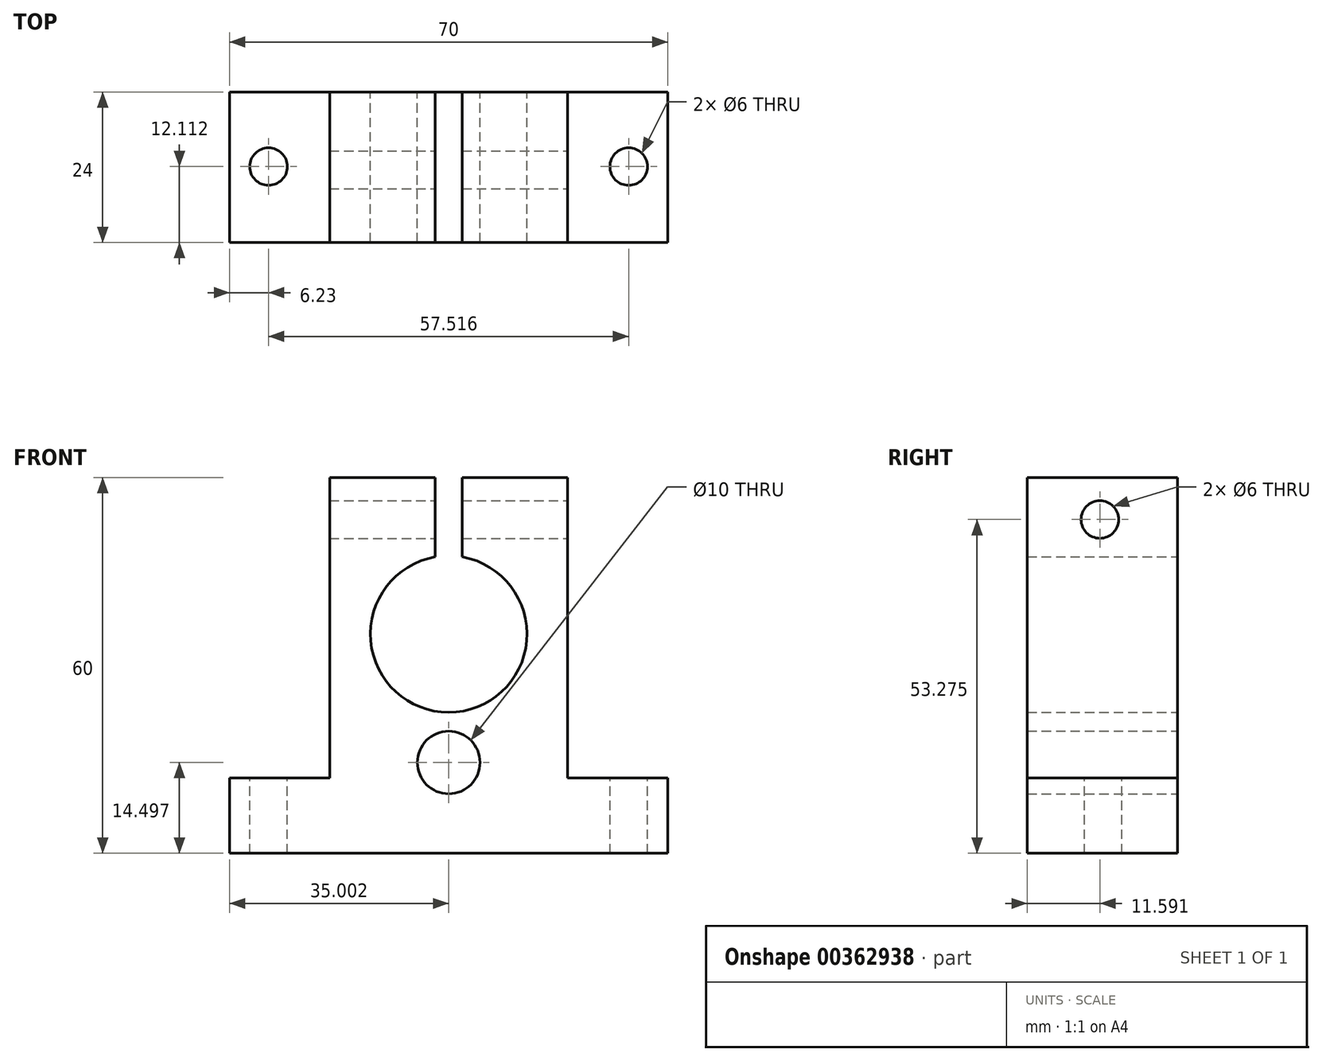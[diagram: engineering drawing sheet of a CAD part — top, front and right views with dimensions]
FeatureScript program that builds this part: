
annotation { "Feature Type Name" : "Feature", "Feature Type Description" : "" }
export const myFeature = defineFeature(function(context is Context, id is Id, definition is map)
    precondition{}
    {
        {
            var Q0;
            Q0=qCreatedBy(makeId("Front.planeOp"),FACE);
            var sketch = newSketch(context, id + "F0", { "sketchPlane" : qUnion([Q0])});
            skLineSegment(sketch, "E0.bottom", {"start": v(1.56, 38.65) * mm, "end": v(18.39, 38.65) * mm});
            skLineSegment(sketch, "E0.top", {"start": v(1.56, -21.35) * mm, "end": v(39.56, -21.35) * mm});
            skLineSegment(sketch, "E0.left", {"start": v(1.56, 38.65) * mm, "end": v(1.56, -9.35) * mm});
            skLineSegment(sketch, "E0.right", {"start": v(39.56, 38.65) * mm, "end": v(39.56, -9.35) * mm});
            skLineSegment(sketch, "E1", {"start": v(1.56, 13.65) * mm, "end": v(20.56, 13.65) * mm, "construction": true});
            skLineSegment(sketch, "E2", {"start": v(20.56, 13.65) * mm, "end": v(39.56, 13.65) * mm, "construction": true});
            skArc(sketch, "E3", {"start": v(18.39, 25.96) * mm, "mid": v(20.56, 1.15) * mm, "end": v(22.74, 25.96) * mm});
            skLineSegment(sketch, "E4", {"start": v(1.56, -21.35) * mm, "end": v(-14.44, -21.35) * mm});
            skLineSegment(sketch, "E5", {"start": v(39.56, -21.35) * mm, "end": v(55.56, -21.35) * mm});
            skLineSegment(sketch, "E6", {"start": v(-14.44, -21.35) * mm, "end": v(-14.44, -9.35) * mm});
            skLineSegment(sketch, "E7", {"start": v(-14.44, -9.35) * mm, "end": v(1.56, -9.35) * mm});
            skLineSegment(sketch, "E8.MirrorCS", {"start": v(55.56, -9.35) * mm, "end": v(39.56, -9.35) * mm});
            skLineSegment(sketch, "E9.MirrorCS", {"start": v(55.56, -21.35) * mm, "end": v(55.56, -9.35) * mm});
            skLineSegment(sketch, "E10", {"start": v(18.39, 38.65) * mm, "end": v(18.39, 25.96) * mm});
            skLineSegment(sketch, "E11.MirrorCS", {"start": v(22.74, 38.65) * mm, "end": v(22.74, 25.96) * mm});
            skLineSegment(sketch, "E12.trimOffspring", {"start": v(22.74, 38.65) * mm, "end": v(39.56, 38.65) * mm});
            skLineSegment(sketch, "E13", {"start": v(20.56, 13.65) * mm, "end": v(20.56, -39.3) * mm, "construction": true});
            skCircle(sketch, "E14", {"center": v(20.56, -6.85) * mm, "radius": 5 * mm});
            skSolve(sketch);
        }
        {
            var Q0;
            Q0=makeQuery(id+"F0.imprint","IMPRINT",FACE,{"disambiguationData":[TD([[makeQuery(id+"F0.imprint","IMPRINT",EDGE,{"derivedFrom":sQuery(id+"F0.wireOp",EDGE,"E0.bottom")}),-1.0]])]});
            extrude(context, id + "F1", {"entities" : qUnion([Q0]), "depth" : 24 * mm});
        }
        {
            var Q0;
            Q0=makeQuery(id+"F1.opExtrude","SWEPT_FACE",FACE,{"disambiguationData":[OSD([sQuery(id+"F0.wireOp",EDGE,"E0.right")])]});
            var sketch = newSketch(context, id + "F2", { "sketchPlane" : qUnion([Q0])});
            skCircle(sketch, "E15", {"center": v(-12.4, 31.93) * mm, "radius": 2.73 * mm});
            skSolve(sketch);
        }
        {
            var Q0;
            Q0=sQuery(id+"F2.wireOp",VERTEX,"E15.center");
            var Q1;
            Q1=makeQuery(id+"F1.opExtrude","SWEPT_BODY",BODY,{"disambiguationData":[OSD([sQuery(id+"F0.wireOp",EDGE,"E0.bottom"),sQuery(id+"F0.wireOp",EDGE,"E0.top"),sQuery(id+"F0.wireOp",EDGE,"E0.left"),sQuery(id+"F0.wireOp",EDGE,"E0.right"),sQuery(id+"F0.wireOp",EDGE,"E3"),sQuery(id+"F0.wireOp",EDGE,"E4"),sQuery(id+"F0.wireOp",EDGE,"E5"),sQuery(id+"F0.wireOp",EDGE,"E6"),sQuery(id+"F0.wireOp",EDGE,"E7"),sQuery(id+"F0.wireOp",EDGE,"E8.MirrorCS"),sQuery(id+"F0.wireOp",EDGE,"E9.MirrorCS"),sQuery(id+"F0.wireOp",EDGE,"E10"),sQuery(id+"F0.wireOp",EDGE,"E11.MirrorCS"),sQuery(id+"F0.wireOp",EDGE,"E12.trimOffspring")])]});
            hole(context, id + "F3", {"style" : HoleStyle.SIMPLE, "endStyle" : HoleEndStyle.THROUGH, "holeDiameter" : 6 * mm, "isTappedThrough" : true, "tappedDepth" : 12 * mm, "tapClearance" : 3, "locations" : qUnion([Q0]), "scope" : qUnion([Q1])});
        }
        {
            var Q0;
            Q0=makeQuery(id+"F1.opExtrude","SWEPT_FACE",FACE,{"disambiguationData":[OSD([sQuery(id+"F0.wireOp",EDGE,"E7")])]});
            var sketch = newSketch(context, id + "F4", { "sketchPlane" : qUnion([Q0])});
            skCircle(sketch, "E16", {"center": v(-8.2, -11.89) * mm, "radius": 3.02 * mm});
            skCircle(sketch, "E17.MirrorC", {"center": v(49.3, -11.89) * mm, "radius": 3.02 * mm});
            skSolve(sketch);
        }
        {
            var Q0;
            Q0=sQuery(id+"F4.wireOp",VERTEX,"E16.center");
            var Q1;
            Q1=sQuery(id+"F4.wireOp",VERTEX,"E17.MirrorC.center");
            var Q2;
            Q2=makeQuery(id+"F1.opExtrude","SWEPT_BODY",BODY,{"disambiguationData":[OSD([sQuery(id+"F0.wireOp",EDGE,"E0.bottom"),sQuery(id+"F0.wireOp",EDGE,"E0.top"),sQuery(id+"F0.wireOp",EDGE,"E0.left"),sQuery(id+"F0.wireOp",EDGE,"E0.right"),sQuery(id+"F0.wireOp",EDGE,"E3"),sQuery(id+"F0.wireOp",EDGE,"E4"),sQuery(id+"F0.wireOp",EDGE,"E5"),sQuery(id+"F0.wireOp",EDGE,"E6"),sQuery(id+"F0.wireOp",EDGE,"E7"),sQuery(id+"F0.wireOp",EDGE,"E8.MirrorCS"),sQuery(id+"F0.wireOp",EDGE,"E9.MirrorCS"),sQuery(id+"F0.wireOp",EDGE,"E10"),sQuery(id+"F0.wireOp",EDGE,"E11.MirrorCS"),sQuery(id+"F0.wireOp",EDGE,"E12.trimOffspring")])]});
            hole(context, id + "F5", {"style" : HoleStyle.SIMPLE, "endStyle" : HoleEndStyle.THROUGH, "holeDiameter" : 6 * mm, "isTappedThrough" : true, "tappedDepth" : 12 * mm, "tapClearance" : 3, "locations" : qUnion([Q0, Q1]), "scope" : qUnion([Q2])});
        }
    });
